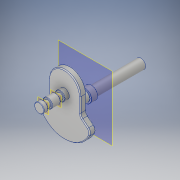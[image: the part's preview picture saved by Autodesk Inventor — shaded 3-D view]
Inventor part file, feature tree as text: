
AUTODESK INVENTOR PART (.ipt)
format: ipt  version: 2018 (Build 220112000, 112)  size: 240,128 bytes
history: native  units: in
note: dims shown in document units (in); Inventor stores cm internally (conversion verified against a paired STEP export)
features: sketch x7, extrude x6, fillet x4, plane x3, chamfer x1, hole x1, thread x1
ambient origin geometry x8: Origin, YZ Plane, XZ Plane, XY Plane, X Axis, Y Axis, Z Axis, Center Point
bodies: Solid1 (feature_tree)
feature tree (23):
  extrude  "Extrusion1"  Depth=0.2in
  fillet  "Fillet1"  Radius=0.073in
  fillet  "Fillet2"  Radius=0.0625in
  extrude  "Extrusion2"  Depth=0.3055in TaperAngle=0.0deg
  plane  "Work Plane1"
  extrude  "Extrusion3"  Depth=0.078in
  plane  "Work Plane2"
  extrude  "Extrusion4"  [1 undecoded]
  chamfer  "Chamfer1"  Distance=0.05in
  extrude  "Extrusion5"  Depth=0.1155in
  hole  "Hole1"  [1 undecoded]
  thread  "Thread1"  [1 undecoded]
  plane  "Work Plane3"
  extrude  "Extrusion6"  Depth=0.0025in
  fillet  "Fillet3"  Radius=0.075in
  fillet  "Fillet4"  Radius=0.0025in
  sketch  "Sketch1"  dims[d6=0.2in d7=0.2in d10=0.073in d11=0.0in d12=0.0625in]
  sketch  "Sketch2"  dims[d13=0.01in d15=0.3055in d16=0.0in]
  sketch  "Sketch3"  dims[d17=-0.05in d18=0.078in]
  sketch  "Sketch4"  dims[d19=0.05in d20=0.0in d21=-0.1in d22=0.05in d23=0.0in]
  sketch  "Sketch5"  dims[d24=0.005in d25=0.125in d26=45.0deg d27=0.1155in]
  sketch  "Sketch6"  dims[d28=0.92in d29=0.0in]
  sketch  "Sketch7"  dims[d30=0.075in d31=0.75in d32=0.1in d33=0.25in d34=45.0deg d35=0.158in d36=0.8108in d37=1.0in d38=0.0in d39=0.175in d40=0.1555in d41=0.075in d42=0.0in d43=0.0025in d44=0.0025in]
note: 3 required parameter values undecoded (feature->parameter linkage not recoverable at this tier; creation-order binding heuristic only, values carry confidence <= 0.55)
